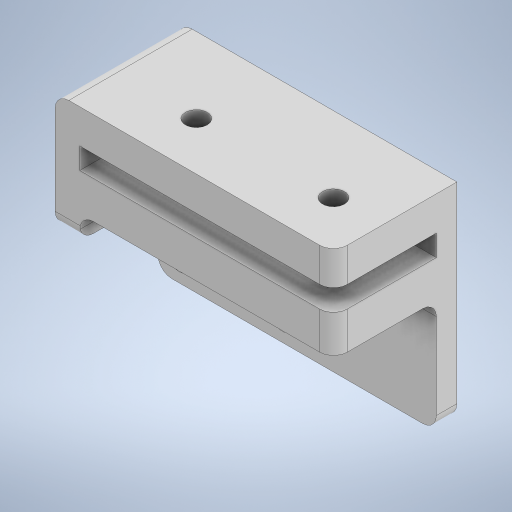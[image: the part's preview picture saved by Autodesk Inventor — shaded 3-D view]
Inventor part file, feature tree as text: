
AUTODESK INVENTOR PART (.ipt)
format: ipt  version: 2024.3 (Build 283343000, 343)  size: 339,456 bytes
history: native  units: mm
features: sketch x7, extrude x5, hole x2, fillet x2, other x1, projected_geometry x1
ambient origin geometry x8: Origin, YZ Plane, XZ Plane, XY Plane, X Axis, Y Axis, Z Axis, Center Point
bodies: Body1 (feature_tree)
feature tree (18):
  other  "ソリッド1"
  extrude  "押し出し1"  Depth=40.0mm
  extrude  "押し出し2"  Depth=30.0mm
  hole  "穴1"  [1 undecoded]
  extrude  "押し出し4"  Depth=3.0mm
  extrude  "押し出し5"  Depth=15.0mm TaperAngle=0.0deg
  extrude  "押し出し7"  Depth=3.0mm
  fillet  "フィレット1"  Radius=3.0mm
  fillet  "フィレット2"  Radius=15.0mm
  hole  "穴3"  [1 undecoded]
  sketch  "スケッチ1"
  sketch  "スケッチ2"
  sketch  "スケッチ5"
  sketch  "スケッチ8"
  sketch  "スケッチ9"
  projected_geometry  "投影ループ1"
  sketch  "スケッチ12"
  sketch  "スケッチ14"
note: 2 required parameter values undecoded (feature->parameter linkage not recoverable at this tier; creation-order binding heuristic only, values carry confidence <= 0.55)
